# Revit family: SRS1
name_source: partatom
category: Lighting Fixtures
revit_build: Autodesk Revit 2013 (Build: 20130531_2115(x64)
units: mm (PartAtom-declared; Revit-internal decimal feet)

## types (1)
- Solitaire SRS1
    Apparent Load = 0 VA
    Arm Material = Metal-Kim Lighting-Aluminum Alloy
    Assembly Code = D5020200
    Color Filter = 16777215
    Default Elevation = 12' - 0"
    Description = Site/Roadway Luminare
    Dimming Lamp Color Temperature Shift = <None>
    Emit Shape Visible in Rendering = No
    Emit from Circle Diameter = 1' - 0"
    Finish = All colors shall be a Super TGIC thermoset polyester powder coat paint, 2.5 mil nominal
thickness
    Full Load Current = 0 A
    Glass Material = Glass-Kim Lighting-Clear
    Housing material = Metal-Kim Lighting-Aluminum Alloy
    Lamp = LED
    Load Classification = Lighting
    Manufacturer = KIM Lighting
    Manufacturer Fax = 626-369-2695
    MasterFormat Title = Parking Lighting, Roadway Lighting, Site Lighting
    Model = SRS1
    Note Text = LF
    Note Visible = Yes
    Number of Poles = 1
    OmniClass Number = 23-80 70 14 21
    OmniClass Title = Street and Roadway Lighting
    Photometric Notes = More IES files download on Photometric Web Link
    Photometric Web File = srs1-2e35-60l3k.ies
    Photometric Web Link = http://www.kimlighting.com
    Pole Material = Metal-Kim Lighting-Aluminum Alloy
    Pole Visible = Yes
    Power Factor = 1
    Product Documentation Link = http://www.kimlighting.com
    Product Page URL = http://www.kimlighting.com
    Revision Date = 11/02/2017
    Series = Solitaire
    Tilt Angle = 90.00°
    Type Comments = Lighting Fixture
    URL = www.kimlighting.com/
    Voltage = 120 V

## geometry (parser evidence)
native form markers: Blend x11, Sweep x4
no freeform markers — native parametric forms only
